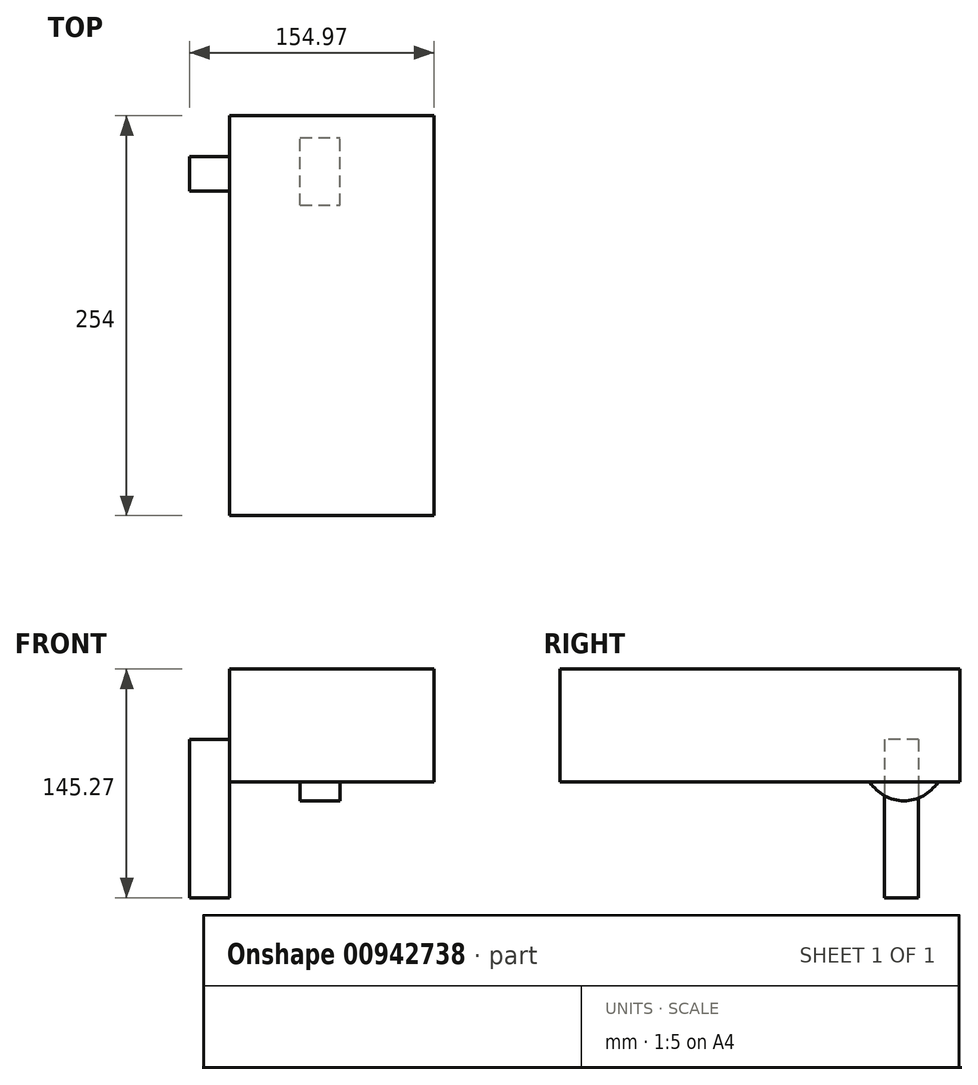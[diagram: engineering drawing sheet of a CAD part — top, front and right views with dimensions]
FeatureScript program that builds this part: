
annotation { "Feature Type Name" : "Feature", "Feature Type Description" : "" }
export const myFeature = defineFeature(function(context is Context, id is Id, definition is map)
    precondition{}
    {
        {
            var Q0;
            Q0=qCreatedBy(makeId("Front.planeOp"),FACE);
            var sketch = newSketch(context, id + "F0", { "sketchPlane" : qUnion([Q0])});
            skLineSegment(sketch, "E0.bottom", {"start": v(-44.78, 44.78) * mm, "end": v(59.4, 44.78) * mm});
            skLineSegment(sketch, "E0.top", {"start": v(-44.78, -26.98) * mm, "end": v(59.4, -26.98) * mm});
            skLineSegment(sketch, "E0.left", {"start": v(-44.78, 44.78) * mm, "end": v(-44.78, -26.98) * mm});
            skLineSegment(sketch, "E0.right", {"start": v(59.4, 44.78) * mm, "end": v(59.4, -26.98) * mm});
            skSolve(sketch);
        }
        {
            var Q0;
            Q0 = qSketchRegion(id + "F0", true);
            extrude(context, id + "F1", {"entities" : qUnion([Q0]), "depth" : 254 * mm, "offsetDistance" : 25.4 * mm});
        }
        {
            var Q0;
            Q0=qCreatedBy(makeId("Right.planeOp"),FACE);
            var sketch = newSketch(context, id + "F2", { "sketchPlane" : qUnion([Q0])});
            skCircle(sketch, "E1", {"center": v(-35.38, -13.4) * mm, "radius": 25.45 * mm});
            skCircle(sketch, "E2", {"center": v(-35.38, -13.4) * mm, "radius": 11.42 * mm});
            skSolve(sketch);
        }
        {
            var Q0;
            Q0=makeQuery(id+"F1.opExtrude","SWEPT_FACE",FACE,{"disambiguationData":[OSD([sQuery(id+"F0.wireOp",EDGE,"E0.left")])]});
            var Q1;
            Q1=makeQuery(id+"F2.imprint","IMPRINT",FACE,{"disambiguationData":[TD([[makeQuery(id+"F2.imprint","IMPRINT",EDGE,{"derivedFrom":sQuery(id+"F2.wireOp",EDGE,"E1")}),1.0]])]});
            extrude(context, id + "F3", {"entities" : qUnion([Q0, Q1]), "operationType" : NewBodyOperationType.ADD, "depth" : 25.4 * mm, "offsetDistance" : 25.4 * mm});
        }
        {
            var Q0;
            Q0=makeQuery(id+"F3.opExtrude","CAP_FACE",FACE,{"disambiguationData":[OSD([sQuery(id+"F0.wireOp",EDGE,"E0.left")])],"isStart":false});
            var sketch = newSketch(context, id + "F4", { "sketchPlane" : qUnion([Q0])});
            skLineSegment(sketch, "E3.bottom", {"start": v(26.1, 0) * mm, "end": v(47.88, 0) * mm});
            skLineSegment(sketch, "E3.top", {"start": v(26.1, -100.49) * mm, "end": v(47.88, -100.49) * mm});
            skLineSegment(sketch, "E3.left", {"start": v(26.1, 0) * mm, "end": v(26.1, -100.49) * mm});
            skLineSegment(sketch, "E3.right", {"start": v(47.88, 0) * mm, "end": v(47.88, -100.49) * mm});
            skSolve(sketch);
        }
        {
            var Q0;
            {var subQ0=sQuery(id+"F4.wireOp",EDGE,"E3.top");Q0=makeQuery(id+"F4.imprint","IMPRINT",FACE,{"disambiguationData":[TD([[makeQuery(id+"F4.imprint","IMPRINT",EDGE,{"derivedFrom":subQ0}),1.0]])]});}
            var Q1;
            {var subQ0=sQuery(id+"F4.wireOp",EDGE,"E3.bottom");Q1=makeQuery(id+"F4.imprint","IMPRINT",FACE,{"disambiguationData":[TD([[makeQuery(id+"F4.imprint","IMPRINT",EDGE,{"derivedFrom":subQ0}),-1.0]])]});}
            extrude(context, id + "F5", {"entities" : qUnion([Q0, Q1]), "operationType" : NewBodyOperationType.ADD, "depth" : 25.4 * mm, "offsetDistance" : 25.4 * mm});
        }
    });
